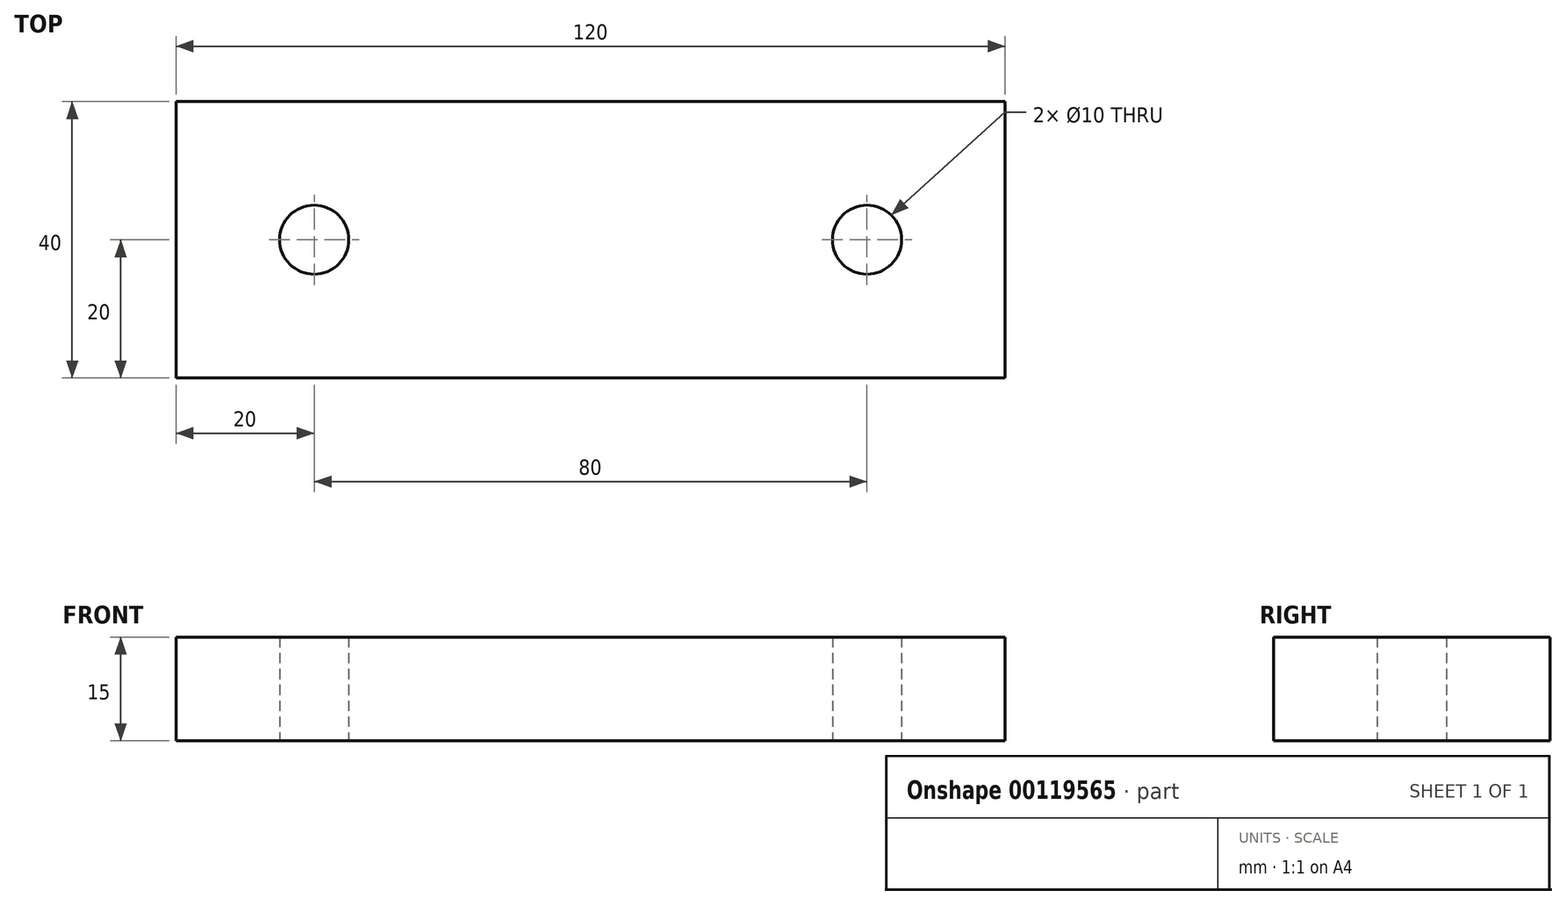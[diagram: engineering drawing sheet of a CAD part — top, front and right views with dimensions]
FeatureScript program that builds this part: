
annotation { "Feature Type Name" : "Feature", "Feature Type Description" : "" }
export const myFeature = defineFeature(function(context is Context, id is Id, definition is map)
    precondition{}
    {
        {
            var Q0;
            Q0=qCreatedBy(makeId("Front.planeOp"),FACE);
            var sketch = newSketch(context, id + "F0", { "sketchPlane" : qUnion([Q0])});
            skLineSegment(sketch, "E0", {"start": v(0, 0) * mm, "end": v(120, 0) * mm});
            skLineSegment(sketch, "E1", {"start": v(120, 0) * mm, "end": v(120, 15) * mm});
            skLineSegment(sketch, "E2", {"start": v(120, 15) * mm, "end": v(0, 15) * mm});
            skLineSegment(sketch, "E3", {"start": v(0, 15) * mm, "end": v(0, 0) * mm});
            skSolve(sketch);
        }
        {
            var Q0;
            Q0 = qSketchRegion(id + "F0", true);
            extrude(context, id + "F1", {"entities" : qUnion([Q0]), "depth" : 40 * mm});
        }
        {
            var Q0;
            Q0=qCreatedBy(makeId("Top.planeOp"),FACE);
            var sketch = newSketch(context, id + "F2", { "sketchPlane" : qUnion([Q0])});
            skCircle(sketch, "E4", {"center": v(20, -20) * mm, "radius": 5 * mm});
            skCircle(sketch, "E5", {"center": v(100, -20) * mm, "radius": 5 * mm});
            skSolve(sketch);
        }
        {
            var Q0;
            Q0 = qSketchRegion(id + "F2", true);
            extrude(context, id + "F3", {"entities" : qUnion([Q0]), "operationType" : NewBodyOperationType.REMOVE, "endBound" : BoundingType.THROUGH_ALL, "depth" : 25 * mm});
        }
    });
